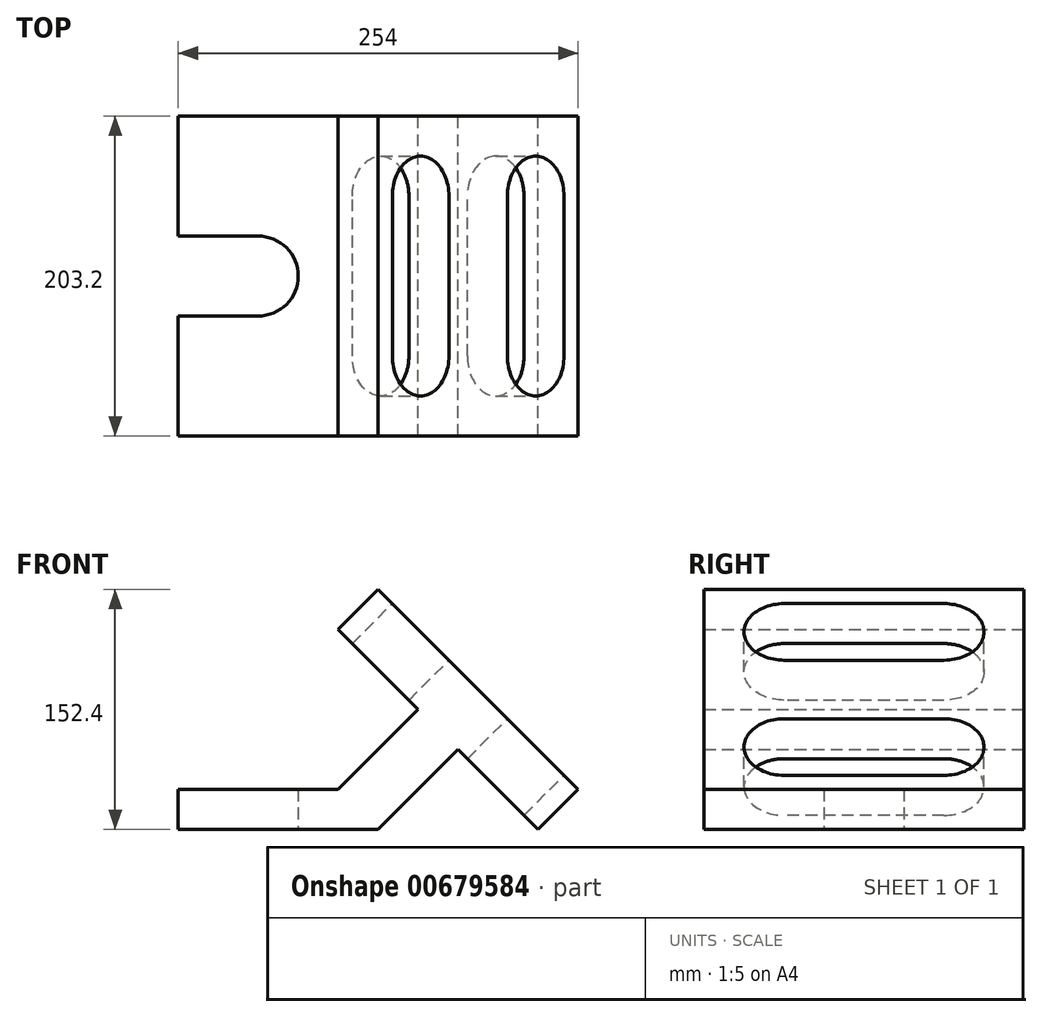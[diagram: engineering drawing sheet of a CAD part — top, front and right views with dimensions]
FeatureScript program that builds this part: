
annotation { "Feature Type Name" : "Feature", "Feature Type Description" : "" }
export const myFeature = defineFeature(function(context is Context, id is Id, definition is map)
    precondition{}
    {
        {
            var Q0;
            Q0=qCreatedBy(makeId("Front.planeOp"),FACE);
            var sketch = newSketch(context, id + "F0", { "sketchPlane" : qUnion([Q0])});
            skLineSegment(sketch, "E0", {"start": v(0, 0) * mm, "end": v(0, 25.4) * mm});
            skLineSegment(sketch, "E1", {"start": v(0, 25.4) * mm, "end": v(101.6, 25.4) * mm});
            skLineSegment(sketch, "E2", {"start": v(101.6, 25.4) * mm, "end": v(101.6, 127) * mm});
            skLineSegment(sketch, "E3", {"start": v(101.6, 127) * mm, "end": v(101.6, 152.4) * mm});
            skLineSegment(sketch, "E4", {"start": v(101.6, 152.4) * mm, "end": v(127, 152.4) * mm});
            skLineSegment(sketch, "E5", {"start": v(127, 152.4) * mm, "end": v(101.6, 127) * mm});
            skLineSegment(sketch, "E6", {"start": v(127, 152.4) * mm, "end": v(254, 152.4) * mm});
            skLineSegment(sketch, "E7", {"start": v(254, 152.4) * mm, "end": v(254, 25.4) * mm});
            skLineSegment(sketch, "E8", {"start": v(254, 25.4) * mm, "end": v(127, 152.4) * mm});
            skLineSegment(sketch, "E9", {"start": v(101.6, 25.4) * mm, "end": v(152.4, 25.4) * mm});
            skLineSegment(sketch, "E10", {"start": v(152.4, 25.4) * mm, "end": v(152.4, 76.2) * mm});
            skLineSegment(sketch, "E11", {"start": v(152.4, 76.2) * mm, "end": v(101.6, 25.4) * mm});
            skLineSegment(sketch, "E12", {"start": v(152.4, 76.2) * mm, "end": v(101.6, 127) * mm});
            skLineSegment(sketch, "E13", {"start": v(0, 0) * mm, "end": v(127, 0) * mm});
            skPoint(sketch, "E13.endSnap0", {"position": v(127, 25.4) * mm});
            skLineSegment(sketch, "E14", {"start": v(127, 0) * mm, "end": v(177.8, 0) * mm});
            skLineSegment(sketch, "E15", {"start": v(177.8, 0) * mm, "end": v(177.8, 50.8) * mm});
            skLineSegment(sketch, "E16", {"start": v(177.8, 50.8) * mm, "end": v(127, 0) * mm});
            skLineSegment(sketch, "E17", {"start": v(177.8, 0) * mm, "end": v(228.6, 0) * mm});
            skLineSegment(sketch, "E18", {"start": v(228.6, 0) * mm, "end": v(254, 25.4) * mm});
            skLineSegment(sketch, "E19", {"start": v(177.8, 50.8) * mm, "end": v(228.6, 0) * mm});
            skSolve(sketch);
        }
        {
            var Q0;
            Q0=makeQuery(id+"F0.imprint","IMPRINT",FACE,{"disambiguationData":[TD([[makeQuery(id+"F0.imprint","IMPRINT",EDGE,{"derivedFrom":sQuery(id+"F0.wireOp",EDGE,"E5")}),1.0]])]});
            var Q1;
            Q1=makeQuery(id+"F0.imprint","IMPRINT",FACE,{"disambiguationData":[TD([[makeQuery(id+"F0.imprint","IMPRINT",EDGE,{"derivedFrom":sQuery(id+"F0.wireOp",EDGE,"E9")}),1.0]])]});
            var Q2;
            Q2=makeQuery(id+"F0.imprint","IMPRINT",FACE,{"disambiguationData":[TD([[makeQuery(id+"F0.imprint","IMPRINT",EDGE,{"derivedFrom":sQuery(id+"F0.wireOp",EDGE,"E0")}),-1.0]])]});
            extrude(context, id + "F1", {"entities" : qUnion([Q0, Q1, Q2]), "endBound" : BoundingType.SYMMETRIC, "depth" : 203.2 * mm, "offsetDistance" : 25.4 * mm});
        }
        {
            var Q0;
            Q0=makeQuery(id+"F1.opExtrude","SWEPT_FACE",FACE,{"disambiguationData":[OSD([sQuery(id+"F0.wireOp",EDGE,"E13")])]});
            var sketch = newSketch(context, id + "F2", { "sketchPlane" : qUnion([Q0])});
            skLineSegment(sketch, "E20", {"start": v(0, 0) * mm, "end": v(0, 25.4) * mm});
            skLineSegment(sketch, "E21", {"start": v(0, 25.4) * mm, "end": v(50.8, 25.4) * mm});
            skLineSegment(sketch, "E22", {"start": v(76.2, 0) * mm, "end": v(76.2, 0) * mm});
            skLineSegment(sketch, "E23", {"start": v(50.8, -25.4) * mm, "end": v(0, -25.4) * mm});
            skLineSegment(sketch, "E24", {"start": v(0, -25.4) * mm, "end": v(0, 0) * mm});
            skPoint(sketch, "E25.visualSharp", {"position": v(76.2, 25.4) * mm});
            skArc(sketch, "E25.filletArc", {"start": v(76.2, 0) * mm, "mid": v(68.76, 17.96) * mm, "end": v(50.8, 25.4) * mm});
            skPoint(sketch, "E26.visualSharp", {"position": v(76.2, -25.4) * mm});
            skArc(sketch, "E26.filletArc", {"start": v(50.8, -25.4) * mm, "mid": v(68.76, -17.96) * mm, "end": v(76.2, 0) * mm});
            skSolve(sketch);
        }
        {
            var Q0;
            Q0=makeQuery(id+"F2.imprint","IMPRINT",FACE,{"disambiguationData":[TD([[makeQuery(id+"F2.imprint","IMPRINT",EDGE,{"derivedFrom":sQuery(id+"F2.wireOp",EDGE,"E20")}),1.0]])]});
            extrude(context, id + "F3", {"entities" : qUnion([Q0]), "operationType" : NewBodyOperationType.REMOVE, "oppositeDirection" : true, "depth" : 25.4 * mm, "offsetDistance" : 25.4 * mm});
        }
        {
            var Q0;
            Q0=makeQuery(id+"F1.opExtrude","SWEPT_FACE",FACE,{"disambiguationData":[OSD([sQuery(id+"F0.wireOp",EDGE,"E8")])]});
            var sketch = newSketch(context, id + "F4", { "sketchPlane" : qUnion([Q0])});
            skLineSegment(sketch, "E27", {"start": v(-101.6, 17.96) * mm, "end": v(-76.2, 17.96) * mm});
            skLineSegment(sketch, "E28", {"start": v(-76.2, 17.96) * mm, "end": v(-76.2, 5.26) * mm});
            skLineSegment(sketch, "E29", {"start": v(-76.2, -20.14) * mm, "end": v(-76.2, -20.14) * mm});
            skLineSegment(sketch, "E30", {"start": v(-50.8, -45.54) * mm, "end": v(50.8, -45.54) * mm});
            skLineSegment(sketch, "E31", {"start": v(76.2, -20.14) * mm, "end": v(76.2, -20.14) * mm});
            skLineSegment(sketch, "E32", {"start": v(50.8, 5.26) * mm, "end": v(-50.8, 5.26) * mm});
            skLineSegment(sketch, "E33", {"start": v(-101.6, -71.84) * mm, "end": v(101.6, -71.84) * mm});
            skPoint(sketch, "E34.visualSharp", {"position": v(-76.2, 5.26) * mm});
            skArc(sketch, "E34.filletArc", {"start": v(-50.8, 5.26) * mm, "mid": v(-68.76, -2.18) * mm, "end": v(-76.2, -20.14) * mm});
            skPoint(sketch, "E35.visualSharp", {"position": v(76.2, 5.26) * mm});
            skArc(sketch, "E35.filletArc", {"start": v(76.2, -20.14) * mm, "mid": v(68.76, -2.18) * mm, "end": v(50.8, 5.26) * mm});
            skPoint(sketch, "E36.visualSharp", {"position": v(76.2, -45.54) * mm});
            skArc(sketch, "E36.filletArc", {"start": v(50.8, -45.54) * mm, "mid": v(68.76, -38.1) * mm, "end": v(76.2, -20.14) * mm});
            skPoint(sketch, "E37.visualSharp", {"position": v(-76.2, -45.54) * mm});
            skArc(sketch, "E37.filletArc", {"start": v(-76.2, -20.14) * mm, "mid": v(-68.76, -38.1) * mm, "end": v(-50.8, -45.54) * mm});
            skLineSegment(sketch, "E38.MirrorCS", {"start": v(-76.2, -161.64) * mm, "end": v(-76.2, -148.94) * mm});
            skArc(sketch, "E39.MirrorCS", {"start": v(76.2, -123.54) * mm, "mid": v(68.76, -141.5) * mm, "end": v(50.8, -148.94) * mm});
            skArc(sketch, "E40.MirrorCS", {"start": v(50.8, -98.14) * mm, "mid": v(68.76, -105.58) * mm, "end": v(76.2, -123.54) * mm});
            skArc(sketch, "E41.MirrorCS", {"start": v(-50.8, -148.94) * mm, "mid": v(-68.76, -141.5) * mm, "end": v(-76.2, -123.54) * mm});
            skArc(sketch, "E42.MirrorCS", {"start": v(-76.2, -123.54) * mm, "mid": v(-68.76, -105.58) * mm, "end": v(-50.8, -98.14) * mm});
            skLineSegment(sketch, "E43.MirrorCS", {"start": v(50.8, -148.94) * mm, "end": v(-50.8, -148.94) * mm});
            skLineSegment(sketch, "E44.MirrorCS", {"start": v(-50.8, -98.14) * mm, "end": v(50.8, -98.14) * mm});
            skLineSegment(sketch, "E45.MirrorCS", {"start": v(76.2, -123.54) * mm, "end": v(76.2, -123.54) * mm});
            skLineSegment(sketch, "E46.MirrorCS", {"start": v(-76.2, -123.54) * mm, "end": v(-76.2, -123.54) * mm});
            skPoint(sketch, "E47.MirrorP", {"position": v(-76.2, -98.14) * mm});
            skPoint(sketch, "E48.MirrorP", {"position": v(76.2, -98.14) * mm});
            skPoint(sketch, "E49.MirrorP", {"position": v(76.2, -148.94) * mm});
            skPoint(sketch, "E50.MirrorP", {"position": v(-76.2, -148.94) * mm});
            skSolve(sketch);
        }
        {
            var Q0;
            Q0 = qSketchRegion(id + "F4", true);
            extrude(context, id + "F5", {"entities" : qUnion([Q0]), "operationType" : NewBodyOperationType.REMOVE, "oppositeDirection" : true, "depth" : 37.85 * mm, "offsetDistance" : 25.4 * mm});
        }
    });
